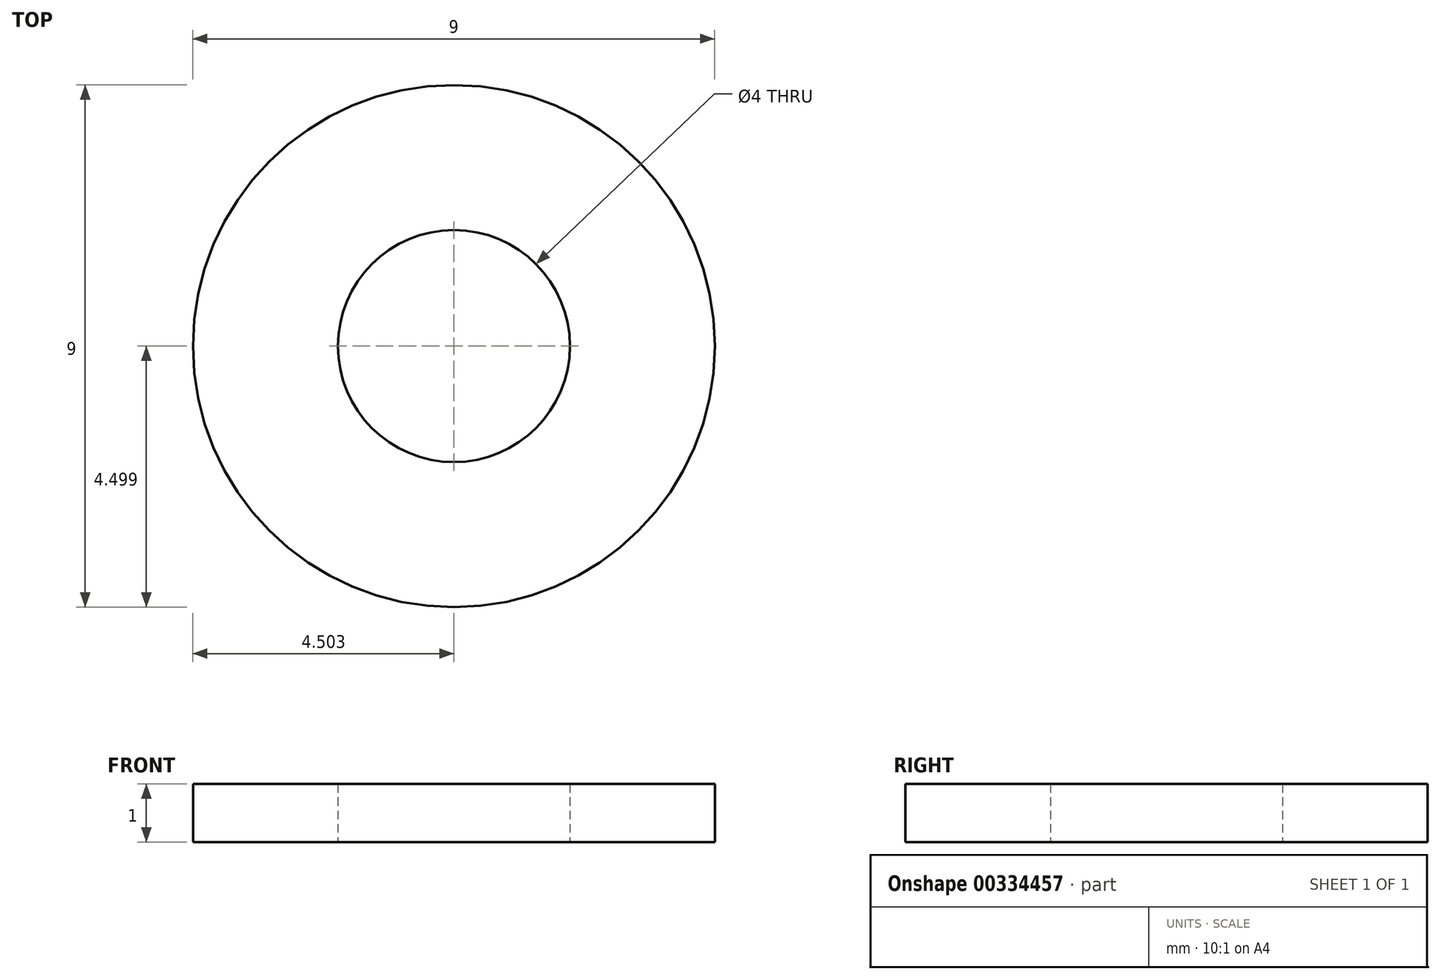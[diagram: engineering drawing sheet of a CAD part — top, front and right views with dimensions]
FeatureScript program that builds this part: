
annotation { "Feature Type Name" : "Feature", "Feature Type Description" : "" }
export const myFeature = defineFeature(function(context is Context, id is Id, definition is map)
    precondition{}
    {
        {
            var Q0;
            Q0=qCreatedBy(makeId("Top.planeOp"),FACE);
            var sketch = newSketch(context, id + "F0", { "sketchPlane" : qUnion([Q0])});
            skCircle(sketch, "E0", {"center": v(-0.05, 0.02) * mm, "radius": 2 * mm});
            skPoint(sketch, "E0.first.point", {"position": v(-2.05, 0) * mm});
            skPoint(sketch, "E0.second.point", {"position": v(1.95, 0) * mm});
            skPoint(sketch, "E0.third.point", {"position": v(0, 2.02) * mm});
            skCircle(sketch, "E1.0", {"center": v(-0.05, 0.02) * mm, "radius": 4.5 * mm});
            skSolve(sketch);
        }
        {
            var Q0;
            Q0=makeQuery(id+"F0.imprint","IMPRINT",FACE,{"disambiguationData":[TD([[makeQuery(id+"F0.imprint","IMPRINT",EDGE,{"derivedFrom":sQuery(id+"F0.wireOp",EDGE,"E0")}),-1.0]])]});
            extrude(context, id + "F1", {"entities" : qUnion([Q0]), "depth" : 1 * mm});
        }
    });
